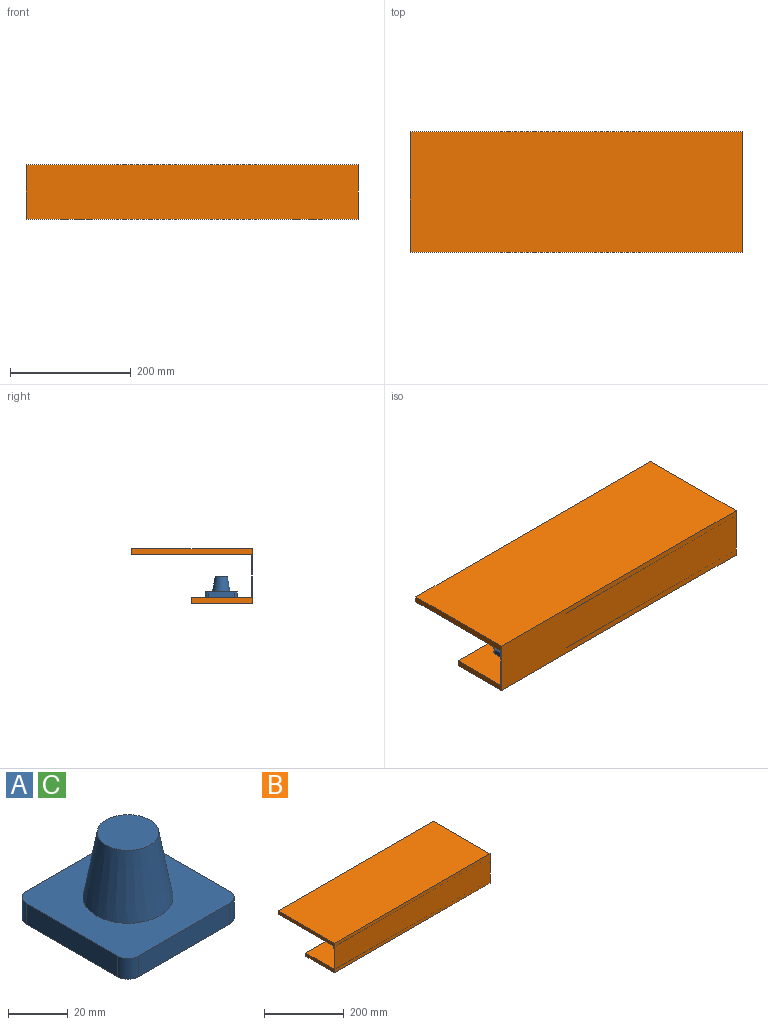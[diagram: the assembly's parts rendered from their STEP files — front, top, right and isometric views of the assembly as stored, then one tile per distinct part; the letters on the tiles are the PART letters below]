
ASSEMBLY  parts=3 mates=2
PART A: 12 faces, bbox 53x53x35 mm
  f0: plane 43x8.5mm, normal (0,-1,0), area 365.5mm2, adj f4,f5,f8,f11
  f1: plane 43x8.5mm, normal (1,0,0), area 365.5mm2, adj f4,f5,f8,f9
  f2: plane 43x8.5mm, normal (0,1,0), area 365.5mm2, adj f4,f5,f9,f10
  f3: plane 43x8.5mm, normal (-1,0,0), area 365.5mm2, adj f4,f5,f10,f11
  f4: plane 53x53mm, normal (0,0,1), area 2080.6mm2, adj f0,f1,f2,f3,f6,f8,f9,f10
  f5: plane 53x53mm, normal (0,0,-1), area 2787.5mm2, adj f0,f1,f2,f3,f8,f9,f10,f11
  f6: cone r=16.5mm half-angle=10deg, axis (0,0,-1), area 2141.3mm2, adj f4,f7
  f7: plane 20.66x20.66mm, normal (0,0,1), area 335.1mm2, adj f6
  f8: cylinder r=5mm len=8.5mm, axis (0,0,1), area 66.8mm2, adj f0,f1,f4,f5
  f9: cylinder r=5mm len=8.5mm, axis (0,0,-1), area 66.8mm2, adj f1,f2,f4,f5
  f10: cylinder r=5mm len=8.5mm, axis (0,0,1), area 66.8mm2, adj f2,f3,f4,f5
  f11: cylinder r=5mm len=8.5mm, axis (0,0,-1), area 66.8mm2, adj f0,f3,f4,f5
PART B: 12 faces, bbox 550x200x90 mm
  f0: plane 200x90mm, normal (-1,0,0), area 3096mm2, adj f1,f4,f6,f7,f8,f9,f10,f11
  f1: plane 550x90mm, normal (0,-1,0), area 49500mm2, adj f0,f2,f7,f10
  f2: plane 200x90mm, normal (1,0,0), area 3096mm2, adj f1,f4,f6,f7,f8,f9,f10,f11
  f3: cylinder r=25mm len=50mm, axis (0,0,-1), area 1570.8mm2, adj f6,f7
  f4: plane 550x10mm, normal (0,1,0), area 5500mm2, adj f0,f2,f6,f7
  f5: cylinder r=25mm len=50mm, axis (0,0,-1), area 1570.8mm2, adj f6,f7
  f6: plane 550x100mm, normal (0,0,1), area 51073mm2, adj f0,f2,f3,f4,f5,f8
  f7: plane 550x101.2mm, normal (0,0,-1), area 51733mm2, adj f0,f1,f2,f3,f4,f5
  f8: plane 550x70mm, normal (0,1,0), area 38500mm2, adj f0,f2,f6,f11
  f9: plane 550x10mm, normal (0,1,0), area 5500mm2, adj f0,f2,f10,f11
  f10: plane 550x200mm, normal (0,0,1), area 110000mm2, adj f0,f1,f2,f9
  f11: plane 550x198.8mm, normal (0,0,-1), area 109340mm2, adj f0,f2,f8,f9
PART C: same geometry as A
PLACE A t=(-191.43,-50,10)mm
PLACE B t=(0,-50,0)mm
PLACE C t=(191.43,-50,10)mm
MATE fastened C.f6 <-> B.f5  axis (0,0,-1) through (191.43,-50,10)mm
MATE fastened A.f6 <-> B.f3  axis (0,0,-1) through (-191.43,-50,10)mm
